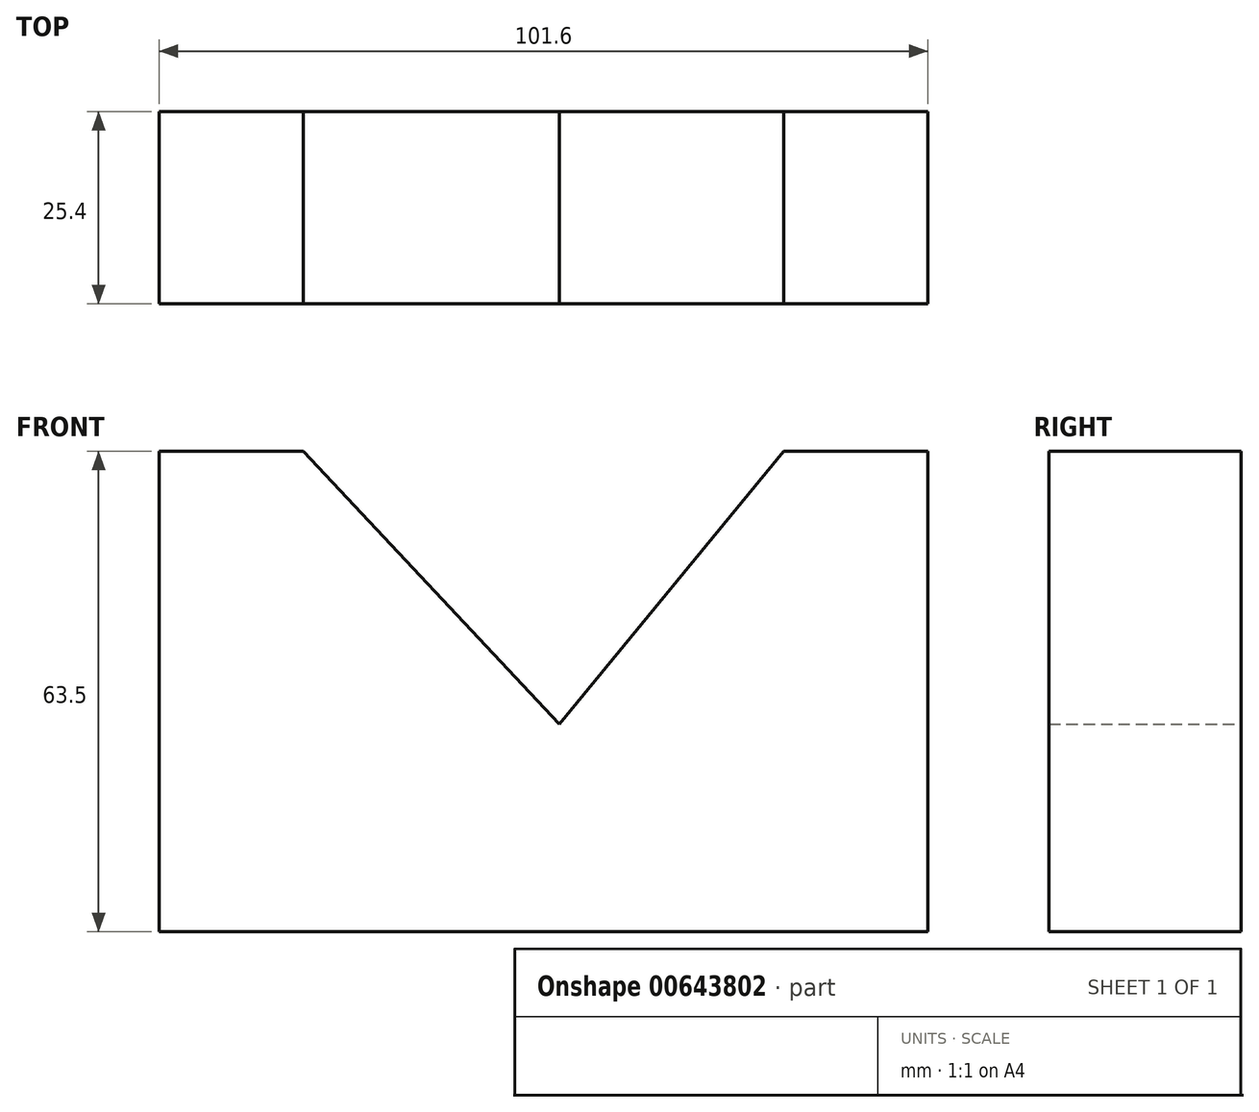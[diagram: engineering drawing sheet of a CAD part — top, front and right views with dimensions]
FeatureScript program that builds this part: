
annotation { "Feature Type Name" : "Feature", "Feature Type Description" : "" }
export const myFeature = defineFeature(function(context is Context, id is Id, definition is map)
    precondition{}
    {
        {
            var Q0;
            Q0=qCreatedBy(makeId("Front.planeOp"),FACE);
            var sketch = newSketch(context, id + "F0", { "sketchPlane" : qUnion([Q0])});
            skLineSegment(sketch, "E0", {"start": v(-75.31, 36.05) * mm, "end": v(-75.31, -27.45) * mm});
            skLineSegment(sketch, "E1", {"start": v(-75.31, -27.45) * mm, "end": v(26.29, -27.45) * mm});
            skLineSegment(sketch, "E2", {"start": v(26.29, -27.45) * mm, "end": v(26.29, 36.05) * mm});
            skLineSegment(sketch, "E3", {"start": v(-75.31, 36.05) * mm, "end": v(-56.26, 36.05) * mm});
            skLineSegment(sketch, "E4", {"start": v(26.29, 36.05) * mm, "end": v(7.24, 36.05) * mm});
            skLineSegment(sketch, "E5", {"start": v(7.24, 36.05) * mm, "end": v(-22.4, 0) * mm});
            skLineSegment(sketch, "E6", {"start": v(-22.4, 0) * mm, "end": v(-56.26, 36.05) * mm});
            skSolve(sketch);
        }
        {
            var Q0;
            Q0=makeQuery(id+"F0.imprint","IMPRINT",FACE,{"disambiguationData":[TD([[makeQuery(id+"F0.imprint","IMPRINT",EDGE,{"derivedFrom":sQuery(id+"F0.wireOp",EDGE,"E0")}),1.0]])]});
            var Q1;
            Q1=makeQuery(id+"F9DTLx1KUj5EF9C_0.imprint","IMPRINT",FACE,{"disambiguationData":[TD([[makeQuery(id+"F9DTLx1KUj5EF9C_0.imprint","IMPRINT",EDGE,{"derivedFrom":sQuery(id+"F9DTLx1KUj5EF9C_0.wireOp",EDGE,"314kEiEX-9Szq-xe4n-Ndq8-LHkLWrVdTdA2")}),1.0]])]});
            extrude(context, id + "F1", {"entities" : qUnion([Q0, Q1]), "depth" : 25.4 * mm, "offsetDistance" : 25.4 * mm});
        }
    });
